# Revit family: RBA4805-711
name_source: partatom
category: Plumbing Fixtures
units: mm (PartAtom-declared; Revit-internal decimal feet)

## family parameters
Always vertical = No
Cut with Voids When Loaded = No
Part Type = Normal
Room Calculation Point = No
Round Connector Dimension = Use Diameter
Shared = No
Work Plane-Based = No

## types (2) — shared parameters
Description = RTA SSS T-Rail Right Hand
Diameter = 32 mm  [stored 0.104987 ft]
Horizontal Rail = Yes
Manufacturer = RBA Group
Materials and Finishes = Brushed Brass
Model = RBA4801-711-RH
Modified Issue = 20161215.01
URL = www.rba.com.au
zero-valued in all types: Default Elevation

## per-type parameters (varying)
| type | Left Hand Rail | Right Hand Rail |
| RBA4805-711-LH | Yes | No |
| RBA4805-711-RH | No | Yes |

note: [stored X ft] marks values corroborated as IEEE doubles in the binary element streams (Revit-internal decimal feet)

## geometry (parser evidence)
native form markers: Blend x4, Sweep x3
no freeform markers — native parametric forms only
